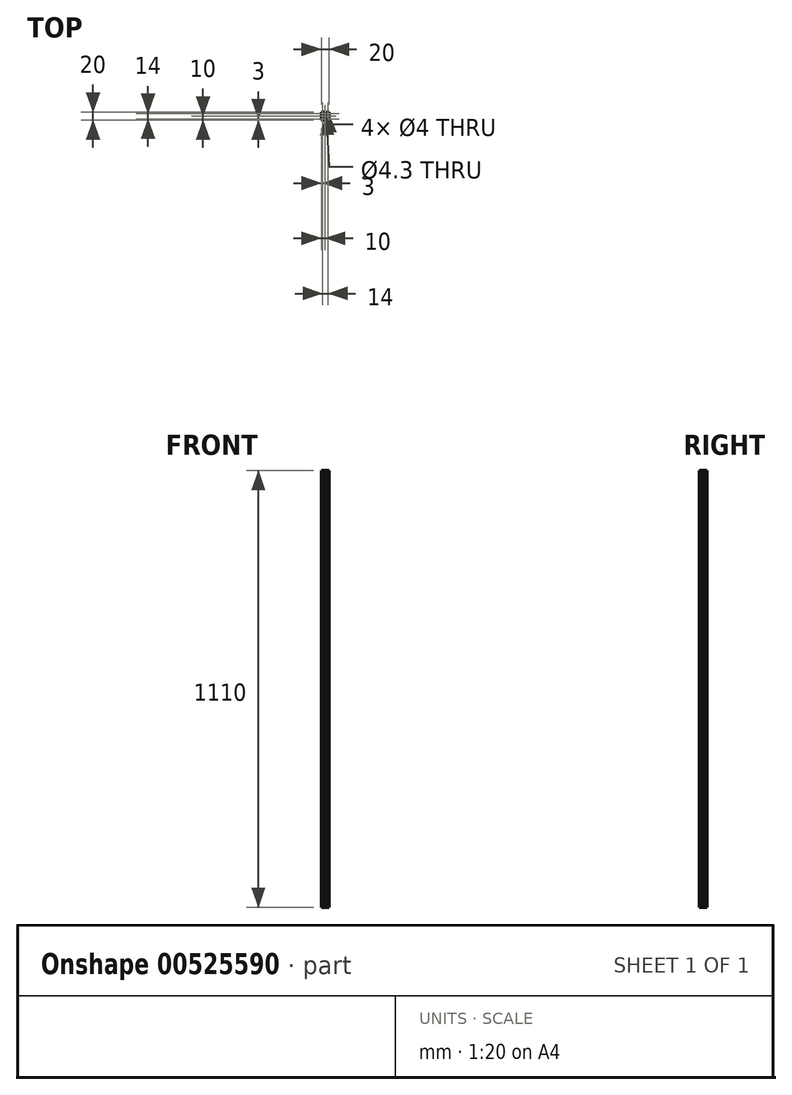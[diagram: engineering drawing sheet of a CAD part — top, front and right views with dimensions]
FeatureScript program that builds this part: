
annotation { "Feature Type Name" : "Feature", "Feature Type Description" : "" }
export const myFeature = defineFeature(function(context is Context, id is Id, definition is map)
    precondition{}
    {
        {
            var Q0;
            Q0=qCreatedBy(makeId("Top.planeOp"),FACE);
            var sketch = newSketch(context, id + "F0", { "sketchPlane" : qUnion([Q0])});
            skCircle(sketch, "E0", {"center": v(-7, 7) * mm, "radius": 2 * mm});
            skCircle(sketch, "E1.MirrorC", {"center": v(-7, -7) * mm, "radius": 2 * mm});
            skLineSegment(sketch, "E2.top", {"start": v(-10, 2.65) * mm, "end": v(-10, -2.65) * mm});
            skLineSegment(sketch, "E2.left", {"start": v(-8.5, 2.65) * mm, "end": v(-10, 2.65) * mm});
            skLineSegment(sketch, "E2.right", {"start": v(-8.5, -2.65) * mm, "end": v(-10, -2.65) * mm});
            skLineSegment(sketch, "E3.bottom", {"start": v(-8.5, 4.15) * mm, "end": v(-8.5, 2.65) * mm});
            skLineSegment(sketch, "E3.left", {"start": v(-8.5, 4.15) * mm, "end": v(-4.55, 4.15) * mm});
            skLineSegment(sketch, "E3.right", {"start": v(-8.5, -4.15) * mm, "end": v(-4.55, -4.15) * mm});
            skArc(sketch, "E4", {"start": v(-4.55, -4.15) * mm, "mid": v(-3.3, 0) * mm, "end": v(-4.55, 4.15) * mm});
            skLineSegment(sketch, "E5.trimOffspring", {"start": v(-8.5, -2.65) * mm, "end": v(-8.5, -4.15) * mm});
            skLineSegment(sketch, "E6.bottom", {"start": v(10, -10) * mm, "end": v(-10, -10) * mm});
            skLineSegment(sketch, "E6.top", {"start": v(10, 10) * mm, "end": v(-10, 10) * mm});
            skLineSegment(sketch, "E6.left", {"start": v(10, -10) * mm, "end": v(10, 10) * mm});
            skLineSegment(sketch, "E6.right", {"start": v(-10, -10) * mm, "end": v(-10, 10) * mm});
            skPoint(sketch, "E6.middle", {"position": v(0, 0) * mm});
            skCircle(sketch, "E7.MirrorC", {"center": v(7, 7) * mm, "radius": 2 * mm});
            skCircle(sketch, "E8.MirrorC", {"center": v(7, -7) * mm, "radius": 2 * mm});
            skLineSegment(sketch, "E9.1.0", {"start": v(-4.15, -8.5) * mm, "end": v(-2.65, -8.5) * mm});
            skArc(sketch, "E9.1.1", {"start": v(4.15, -4.55) * mm, "mid": v(0, -3.3) * mm, "end": v(-4.15, -4.55) * mm});
            skLineSegment(sketch, "E9.1.2", {"start": v(-2.65, -10) * mm, "end": v(2.65, -10) * mm});
            skLineSegment(sketch, "E9.1.3", {"start": v(-2.65, -8.5) * mm, "end": v(-2.65, -10) * mm});
            skLineSegment(sketch, "E9.1.4", {"start": v(-4.15, -8.5) * mm, "end": v(-4.15, -4.55) * mm});
            skLineSegment(sketch, "E9.1.5", {"start": v(2.65, -8.5) * mm, "end": v(4.15, -8.5) * mm});
            skLineSegment(sketch, "E9.1.6", {"start": v(4.15, -8.5) * mm, "end": v(4.15, -4.55) * mm});
            skLineSegment(sketch, "E9.1.7", {"start": v(2.65, -8.5) * mm, "end": v(2.65, -10) * mm});
            skLineSegment(sketch, "E9.2.0", {"start": v(8.5, -4.15) * mm, "end": v(8.5, -2.65) * mm});
            skArc(sketch, "E9.2.1", {"start": v(4.55, 4.15) * mm, "mid": v(3.3, 0) * mm, "end": v(4.55, -4.15) * mm});
            skLineSegment(sketch, "E9.2.2", {"start": v(10, -2.65) * mm, "end": v(10, 2.65) * mm});
            skLineSegment(sketch, "E9.2.3", {"start": v(8.5, -2.65) * mm, "end": v(10, -2.65) * mm});
            skLineSegment(sketch, "E9.2.4", {"start": v(8.5, -4.15) * mm, "end": v(4.55, -4.15) * mm});
            skLineSegment(sketch, "E9.2.5", {"start": v(8.5, 2.65) * mm, "end": v(8.5, 4.15) * mm});
            skLineSegment(sketch, "E9.2.6", {"start": v(8.5, 4.15) * mm, "end": v(4.55, 4.15) * mm});
            skLineSegment(sketch, "E9.2.7", {"start": v(8.5, 2.65) * mm, "end": v(10, 2.65) * mm});
            skLineSegment(sketch, "E9.3.0", {"start": v(4.15, 8.5) * mm, "end": v(2.65, 8.5) * mm});
            skArc(sketch, "E9.3.1", {"start": v(-4.15, 4.55) * mm, "mid": v(0, 3.3) * mm, "end": v(4.15, 4.55) * mm});
            skLineSegment(sketch, "E9.3.2", {"start": v(2.65, 10) * mm, "end": v(-2.65, 10) * mm});
            skLineSegment(sketch, "E9.3.3", {"start": v(2.65, 8.5) * mm, "end": v(2.65, 10) * mm});
            skLineSegment(sketch, "E9.3.4", {"start": v(4.15, 8.5) * mm, "end": v(4.15, 4.55) * mm});
            skLineSegment(sketch, "E9.3.5", {"start": v(-2.65, 8.5) * mm, "end": v(-4.15, 8.5) * mm});
            skLineSegment(sketch, "E9.3.6", {"start": v(-4.15, 8.5) * mm, "end": v(-4.15, 4.55) * mm});
            skLineSegment(sketch, "E9.3.7", {"start": v(-2.65, 8.5) * mm, "end": v(-2.65, 10) * mm});
            skCircle(sketch, "E10", {"center": v(0, 0) * mm, "radius": 2.15 * mm});
            skSolve(sketch);
        }
        {
            var Q0;
            Q0=makeQuery(id+"F0.imprint","IMPRINT",FACE,{"disambiguationData":[TD([[makeQuery(id+"F0.imprint","IMPRINT",EDGE,{"derivedFrom":sQuery(id+"F0.wireOp",EDGE,"E0")}),-1.0]])]});
            extrude(context, id + "F1", {"entities" : qUnion([Q0]), "depth" : 1110 * mm, "offsetDistance" : 25 * mm});
        }
    });
